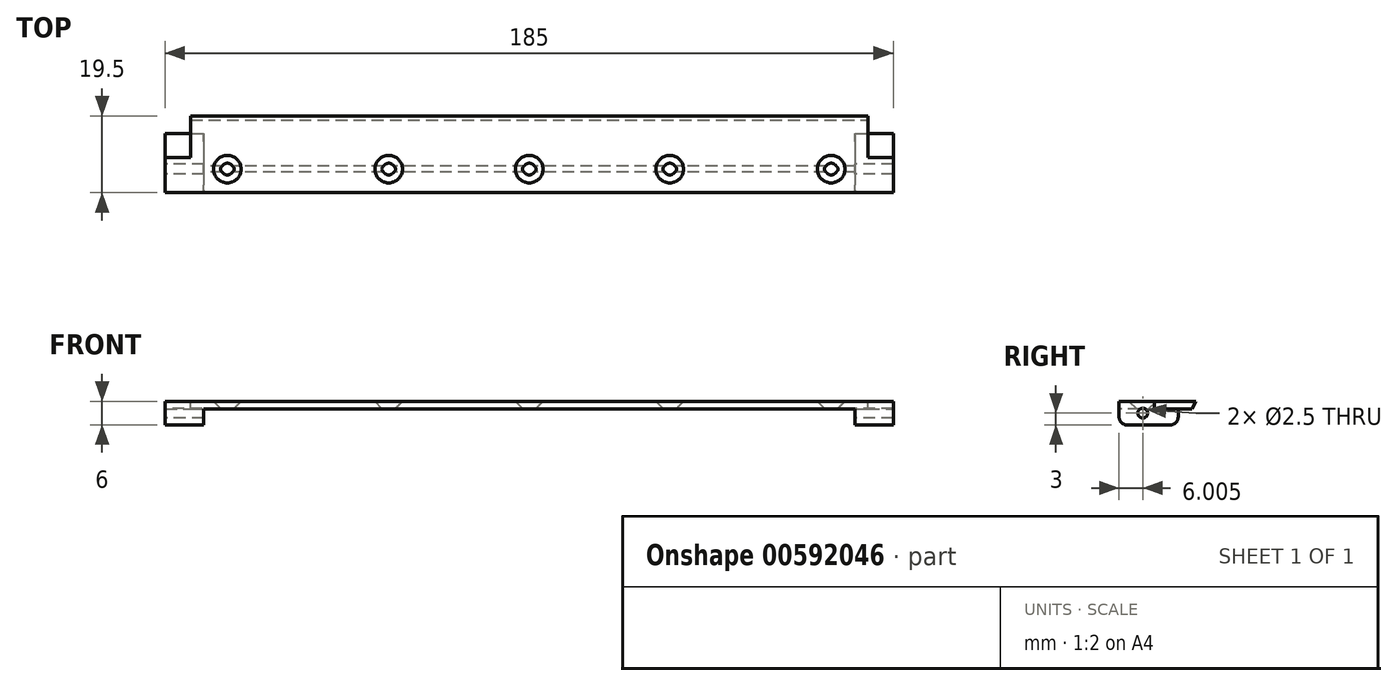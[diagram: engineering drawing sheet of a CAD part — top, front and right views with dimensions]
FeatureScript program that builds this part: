
annotation { "Feature Type Name" : "Feature", "Feature Type Description" : "" }
export const myFeature = defineFeature(function(context is Context, id is Id, definition is map)
    precondition{}
    {
        {
            var Q0;
            Q0=qCreatedBy(makeId("Top.planeOp"),FACE);
            var sketch = newSketch(context, id + "F0", { "sketchPlane" : qUnion([Q0])});
            skLineSegment(sketch, "E0.bottom", {"start": v(-95.15, 6.98) * mm, "end": v(89.85, 6.98) * mm});
            skLineSegment(sketch, "E0.top", {"start": v(-95.15, -8.02) * mm, "end": v(89.85, -8.02) * mm});
            skLineSegment(sketch, "E0.left", {"start": v(-95.15, 6.98) * mm, "end": v(-95.15, -8.02) * mm});
            skLineSegment(sketch, "E0.right", {"start": v(89.85, 6.98) * mm, "end": v(89.85, -8.02) * mm});
            skLineSegment(sketch, "E1", {"start": v(-85.35, 6.98) * mm, "end": v(-85.35, -8.02) * mm});
            skLineSegment(sketch, "E2", {"start": v(80.05, 6.98) * mm, "end": v(80.05, -8.02) * mm});
            skSolve(sketch);
        }
        {
            var Q0;
            {var subQ0=sQuery(id+"F0.wireOp",EDGE,"E1");Q0=makeQuery(id+"F0.imprint","IMPRINT",FACE,{"disambiguationData":[TD([[makeQuery(id+"F0.imprint","IMPRINT",EDGE,{"derivedFrom":subQ0}),1.0]])]});}
            var Q1;
            {var subQ0=sQuery(id+"F0.wireOp",EDGE,"E0.left");Q1=makeQuery(id+"F0.imprint","IMPRINT",FACE,{"disambiguationData":[TD([[makeQuery(id+"F0.imprint","IMPRINT",EDGE,{"derivedFrom":subQ0}),1.0]])]});}
            var Q2;
            {var subQ0=sQuery(id+"F0.wireOp",EDGE,"E0.right");Q2=makeQuery(id+"F0.imprint","IMPRINT",FACE,{"disambiguationData":[TD([[makeQuery(id+"F0.imprint","IMPRINT",EDGE,{"derivedFrom":subQ0}),-1.0]])]});}
            extrude(context, id + "F1", {"entities" : qUnion([Q0, Q1, Q2]), "depth" : 6 * mm, "offsetDistance" : 25 * mm});
        }
        {
            var Q0;
            {var subQ0=sQuery(id+"F0.wireOp",EDGE,"E1");Q0=makeQuery(id+"F0.imprint","IMPRINT",FACE,{"disambiguationData":[TD([[makeQuery(id+"F0.imprint","IMPRINT",EDGE,{"derivedFrom":subQ0}),1.0]])]});}
            extrude(context, id + "F2", {"entities" : qUnion([Q0]), "operationType" : NewBodyOperationType.REMOVE, "depth" : 4 * mm, "offsetDistance" : 25 * mm});
        }
        {
            var Q0;
            Q0=makeQuery(id+"F1.opExtrude","SWEPT_FACE",FACE,{"disambiguationData":[OSD([sQuery(id+"F0.wireOp",EDGE,"E0.left")])]});
            var sketch = newSketch(context, id + "F3", { "sketchPlane" : qUnion([Q0])});
            skPoint(sketch, "E3", {"position": v(2.02, 3) * mm});
            skSolve(sketch);
        }
        {
            var Q0;
            Q0=sQuery(id+"F3.wireOp",VERTEX,"E3");
            var Q1;
            Q1=makeQuery(id+"F1.opExtrude","SWEPT_BODY",BODY,{"disambiguationData":[OSD([sQuery(id+"F0.wireOp",EDGE,"E0.bottom"),sQuery(id+"F0.wireOp",EDGE,"E0.top"),sQuery(id+"F0.wireOp",EDGE,"E0.left"),sQuery(id+"F0.wireOp",EDGE,"E0.right")])]});
            hole(context, id + "F4", {"style" : HoleStyle.SIMPLE, "endStyle" : HoleEndStyle.BLIND, "holeDiameter" : 2.5 * mm, "majorDiameter" : 5 * mm, "holeDepth" : 200 * mm, "isTappedThrough" : true, "tappedDepth" : 12 * mm, "tapClearance" : 3, "locations" : qUnion([Q0]), "scope" : qUnion([Q1])});
        }
        {
            var Q0;
            {var subQ0=sQuery(id+"F0.wireOp",EDGE,"E0.bottom");var subQ1=sQuery(id+"F0.wireOp",EDGE,"E0.right");Q0=makeQuery(id+"F2.boolean.opBoolean","SPLIT",EDGE,{"disambiguationData":[TD([makeQuery(id+"F1.opExtrude","SWEPT_FACE",FACE,{"disambiguationData":[OSD([subQ1])]})])],"derivedFrom":makeQuery(id+"F1.opExtrude","CAP_EDGE",EDGE,{"disambiguationData":[OSD([subQ0])],"isStart":true})});}
            var Q1;
            {var subQ0=sQuery(id+"F0.wireOp",EDGE,"E0.left");var subQ1=sQuery(id+"F0.wireOp",EDGE,"E0.top");Q1=makeQuery(id+"F2.boolean.opBoolean","SPLIT",EDGE,{"disambiguationData":[TD([makeQuery(id+"F1.opExtrude","SWEPT_FACE",FACE,{"disambiguationData":[OSD([subQ0])]})])],"derivedFrom":makeQuery(id+"F1.opExtrude","CAP_EDGE",EDGE,{"disambiguationData":[OSD([subQ1])],"isStart":true})});}
            var Q2;
            {var subQ0=sQuery(id+"F0.wireOp",EDGE,"E0.right");var subQ1=sQuery(id+"F0.wireOp",EDGE,"E0.top");Q2=makeQuery(id+"F2.boolean.opBoolean","SPLIT",EDGE,{"disambiguationData":[TD([makeQuery(id+"F1.opExtrude","SWEPT_FACE",FACE,{"disambiguationData":[OSD([subQ0])]})])],"derivedFrom":makeQuery(id+"F1.opExtrude","CAP_EDGE",EDGE,{"disambiguationData":[OSD([subQ1])],"isStart":true})});}
            var Q3;
            {var subQ0=sQuery(id+"F0.wireOp",EDGE,"E0.bottom");var subQ1=sQuery(id+"F0.wireOp",EDGE,"E0.left");Q3=makeQuery(id+"F2.boolean.opBoolean","SPLIT",EDGE,{"disambiguationData":[TD([makeQuery(id+"F1.opExtrude","SWEPT_FACE",FACE,{"disambiguationData":[OSD([subQ1])]})])],"derivedFrom":makeQuery(id+"F1.opExtrude","CAP_EDGE",EDGE,{"disambiguationData":[OSD([subQ0])],"isStart":true})});}
            fillet(context, id + "F5", {"entities" : qUnion([Q0, Q1, Q2, Q3]), "radius" : 2 * mm, "tangentPropagation" : true, "allowEdgeOverflow" : false});
        }
        {
            var Q0;
            {var subQ0=sQuery(id+"F0.wireOp",EDGE,"E1");Q0=makeQuery(id+"F0.imprint","IMPRINT",FACE,{"disambiguationData":[TD([[makeQuery(id+"F0.imprint","IMPRINT",EDGE,{"derivedFrom":subQ0}),1.0]])]});}
            var sketch = newSketch(context, id + "F6", { "sketchPlane" : qUnion([Q0])});
            skLineSegment(sketch, "E4", {"start": v(-85.35, -2.02) * mm, "end": v(80.05, -2.02) * mm, "construction": true});
            skPoint(sketch, "E5", {"position": v(-79.35, -2.02) * mm});
            skPoint(sketch, "E6", {"position": v(-2.65, -2.02) * mm});
            skPoint(sketch, "E7", {"position": v(74.05, -2.02) * mm});
            skPoint(sketch, "E8", {"position": v(-38.35, -2.02) * mm});
            skPoint(sketch, "E9", {"position": v(33.05, -2.02) * mm});
            skSolve(sketch);
        }
        {
            var Q0;
            Q0=makeQuery(id+"F1.opExtrude","CAP_FACE",FACE,{"disambiguationData":[OSD([sQuery(id+"F0.wireOp",EDGE,"E0.bottom"),sQuery(id+"F0.wireOp",EDGE,"E0.top"),sQuery(id+"F0.wireOp",EDGE,"E0.left"),sQuery(id+"F0.wireOp",EDGE,"E0.right")])],"isStart":false});
            var sketch = newSketch(context, id + "F7", { "sketchPlane" : qUnion([Q0])});
            skLineSegment(sketch, "E10", {"start": v(-95.15, 0.98) * mm, "end": v(-88.65, 0.98) * mm});
            skLineSegment(sketch, "E11", {"start": v(-88.65, 0.98) * mm, "end": v(-88.65, 6.98) * mm});
            skLineSegment(sketch, "E12", {"start": v(89.85, 0.98) * mm, "end": v(83.35, 0.98) * mm});
            skLineSegment(sketch, "E13", {"start": v(83.35, 0.98) * mm, "end": v(83.35, 6.98) * mm});
            skSolve(sketch);
        }
        {
            var Q0;
            {var subQ0=sQuery(id+"F7.wireOp",EDGE,"E10");Q0=makeQuery(id+"F7.imprint","IMPRINT",FACE,{"disambiguationData":[TD([[makeQuery(id+"F7.imprint","IMPRINT",EDGE,{"derivedFrom":subQ0}),1.0]])]});}
            var Q1;
            {var subQ0=sQuery(id+"F7.wireOp",EDGE,"E12");Q1=makeQuery(id+"F7.imprint","IMPRINT",FACE,{"disambiguationData":[TD([[makeQuery(id+"F7.imprint","IMPRINT",EDGE,{"derivedFrom":subQ0}),-1.0]])]});}
            extrude(context, id + "F8", {"entities" : qUnion([Q0, Q1]), "operationType" : NewBodyOperationType.REMOVE, "oppositeDirection" : true, "depth" : 2 * mm, "offsetDistance" : 25 * mm});
        }
        {
            var Q0;
            Q0=makeQuery(id+"F1.opExtrude","SWEPT_FACE",FACE,{"disambiguationData":[OSD([sQuery(id+"F0.wireOp",EDGE,"E0.bottom")])]});
            var sketch = newSketch(context, id + "F9", { "sketchPlane" : qUnion([Q0])});
            skLineSegment(sketch, "E14.bottom", {"start": v(-83.35, 4) * mm, "end": v(88.65, 4) * mm});
            skLineSegment(sketch, "E14.top", {"start": v(-83.35, 6) * mm, "end": v(88.65, 6) * mm});
            skLineSegment(sketch, "E14.left", {"start": v(-83.35, 4) * mm, "end": v(-83.35, 6) * mm});
            skLineSegment(sketch, "E14.right", {"start": v(88.65, 4) * mm, "end": v(88.65, 6) * mm});
            skSolve(sketch);
        }
        {
            var Q0;
            Q0 = qSketchRegion(id + "F9", true);
            extrude(context, id + "F10", {"entities" : qUnion([Q0]), "operationType" : NewBodyOperationType.ADD, "depth" : 5 * mm, "offsetDistance" : 25 * mm});
        }
        {
            var Q0;
            Q0=makeQuery(id+"F10.opExtrude","CAP_EDGE",EDGE,{"disambiguationData":[OSD([sQuery(id+"F9.wireOp",EDGE,"E14.bottom")])],"isStart":false});
            chamfer(context, id + "F11", {"entities" : qUnion([Q0]), "chamferType" : ChamferType.TWO_OFFSETS, "width1" : 1.5 * mm, "oppositeDirection" : false, "width2" : 3 * mm, "tangentPropagation" : true});
        }
        {
            var Q0;
            Q0=makeQuery(id+"F10.boolean.opBoolean","MERGE",FACE,{"derivedFrom":[makeQuery(id+"F1.opExtrude","CAP_FACE",FACE,{"disambiguationData":[OSD([sQuery(id+"F0.wireOp",EDGE,"E0.bottom"),sQuery(id+"F0.wireOp",EDGE,"E0.top"),sQuery(id+"F0.wireOp",EDGE,"E0.left"),sQuery(id+"F0.wireOp",EDGE,"E0.right")])],"isStart":false}),makeQuery(id+"F10.opExtrude","SWEPT_FACE",FACE,{"disambiguationData":[OSD([sQuery(id+"F9.wireOp",EDGE,"E14.top")])]})]});
            var sketch = newSketch(context, id + "F12", { "sketchPlane" : qUnion([Q0])});
            skPoint(sketch, "E15", {"position": v(-79.35, -2.02) * mm});
            skPoint(sketch, "E16", {"position": v(-38.35, -2.02) * mm});
            skPoint(sketch, "E17", {"position": v(-2.65, -2.02) * mm});
            skPoint(sketch, "E18", {"position": v(33.05, -2.02) * mm});
            skPoint(sketch, "E19", {"position": v(74.05, -2.02) * mm});
            skSolve(sketch);
        }
        {
            var Q0;
            Q0=sQuery(id+"F12.wireOp",VERTEX,"E15");
            var Q1;
            Q1=sQuery(id+"F12.wireOp",VERTEX,"E16");
            var Q2;
            Q2=sQuery(id+"F12.wireOp",VERTEX,"E17");
            var Q3;
            Q3=sQuery(id+"F12.wireOp",VERTEX,"E18");
            var Q4;
            Q4=sQuery(id+"F12.wireOp",VERTEX,"E19");
            var Q5;
            Q5=makeQuery(id+"F1.opExtrude","SWEPT_BODY",BODY,{"disambiguationData":[OSD([sQuery(id+"F0.wireOp",EDGE,"E0.bottom"),sQuery(id+"F0.wireOp",EDGE,"E0.top"),sQuery(id+"F0.wireOp",EDGE,"E0.left"),sQuery(id+"F0.wireOp",EDGE,"E0.right")])]});
            hole(context, id + "F13", {"style" : HoleStyle.C_SINK, "endStyle" : HoleEndStyle.BLIND, "holeDiameter" : 3 * mm, "cSinkDiameter" : 7 * mm, "cSinkAngle" : 90 * degree, "majorDiameter" : 5 * mm, "holeDepth" : 4 * mm, "isTappedThrough" : true, "tappedDepth" : 12 * mm, "tapClearance" : 3, "locations" : qUnion([Q0, Q1, Q2, Q3, Q4]), "scope" : qUnion([Q5])});
        }
    });
